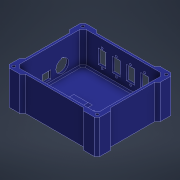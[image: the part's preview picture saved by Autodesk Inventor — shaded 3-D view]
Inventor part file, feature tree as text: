
AUTODESK INVENTOR PART (.ipt)
format: ipt  version: 2021.3 (Build 253353000, 353)  size: 437,760 bytes
history: native  units: mm
features: projected_geometry x15, sketch x9, extrude x6, hole x3, chamfer x2
ambient origin geometry x8: Origin, YZ Plane, XZ Plane, XY Plane, X Axis, Y Axis, Z Axis, Center Point
bodies: Body1 (feature_tree)
feature tree (35):
  extrude  "Extrusion2"  Depth=100.0mm
  extrude  "Extrusion3"  Depth=15.0mm
  extrude  "Extrusion4"  Depth=4.0mm
  chamfer  "Chamfer1"  Distance=3.0mm
  hole  "Hole1"  [1 undecoded]
  extrude  "Extrusion5"  Depth=45.0mm
  hole  "Hole2"  [1 undecoded]
  extrude  "Extrusion6"  Depth=14.0mm
  extrude  "Extrusion7"  Depth=2.0mm
  hole  "Hole3"  [1 undecoded]
  chamfer  "Chamfer2"  Distance=2.5mm
  sketch  "Sketch1"  dims[d4=120.0mm d5=100.0mm]
  sketch  "Sketch2"  dims[d6=45.0deg d7=15.0mm]
  projected_geometry  "Projected Loop1"
  sketch  "Sketch4"  dims[d8=4.0mm d9=4.0mm]
  projected_geometry  "Projected Loop2"
  projected_geometry  "Projected Loop3"
  sketch  "Sketch5"  dims[d12=45.0deg]
  projected_geometry  "Projected Loop4"
  projected_geometry  "Projected Loop5"
  sketch  "Sketch6"  dims[d13=4.0mm d14=3.0mm d15=0.0mm]
  projected_geometry  "Projected Loop6"
  projected_geometry  "Projected Loop7"
  projected_geometry  "Projected Loop8"
  projected_geometry  "Projected Loop9"
  projected_geometry  "Projected Loop10"
  sketch  "Sketch7"  dims[d16=3.0mm d17=10.0mm]
  projected_geometry  "Projected Loop11"
  sketch  "Sketch8"  dims[d18=45.0mm d19=0.0mm d20=53.34mm]
  projected_geometry  "Projected Loop12"
  projected_geometry  "Projected Loop13"
  sketch  "Sketch10"  dims[d21=101.6mm d23=5.0mm]
  projected_geometry  "Projected Loop14"
  sketch  "Sketch11"  dims[d24=3.0mm d25=14.0mm d26=1.3mm d27=50.8mm d29=2.5mm d30=5.1mm d31=27.9mm d32=15.2mm d33=24.1mm d34=96.52mm d35=30.0mm d36=50.0mm d37=10.0mm d38=10.0mm d39=75.0mm d40=85.0mm d41=5.0mm d42=3.0mm d43=0.0mm d44=3.0mm d45=2.0mm d46=45.0deg d47=4.0mm d48=6.0mm d49=4.0mm d50=2.0mm d51=90.0deg d52=5.0mm d53=0.0mm d55=11.5mm d56=12.5mm d57=1.7mm d58=9.25mm d59=10.0mm d60=0.0mm d61=4.0mm d62=6.0mm d63=4.0mm d64=2.0mm d65=90.0deg d66=5.0mm d67=0.0mm d68=18.0mm d69=20.0mm d70=3.0mm d71=13.0mm d72=13.0mm d73=10.0mm d74=0.0mm d75=13.0mm d76=11.0mm d77=31.0mm d78=20.0mm d79=40.0mm d81=20.0mm d82=10.0mm d84=10.0mm d86=5.0mm d87=0.0mm d88=25.0mm d89=40.0mm d91=20.0mm d92=10.0mm d94=10.0mm d96=2.9mm d97=6.0mm d98=5.5mm d99=2.9mm d100=90.0deg d101=3.0mm d102=0.0mm d103=2.0mm d104=2.0mm d105=45.0deg]
  projected_geometry  "Projected Loop15"
note: 3 required parameter values undecoded (feature->parameter linkage not recoverable at this tier; creation-order binding heuristic only, values carry confidence <= 0.55)
